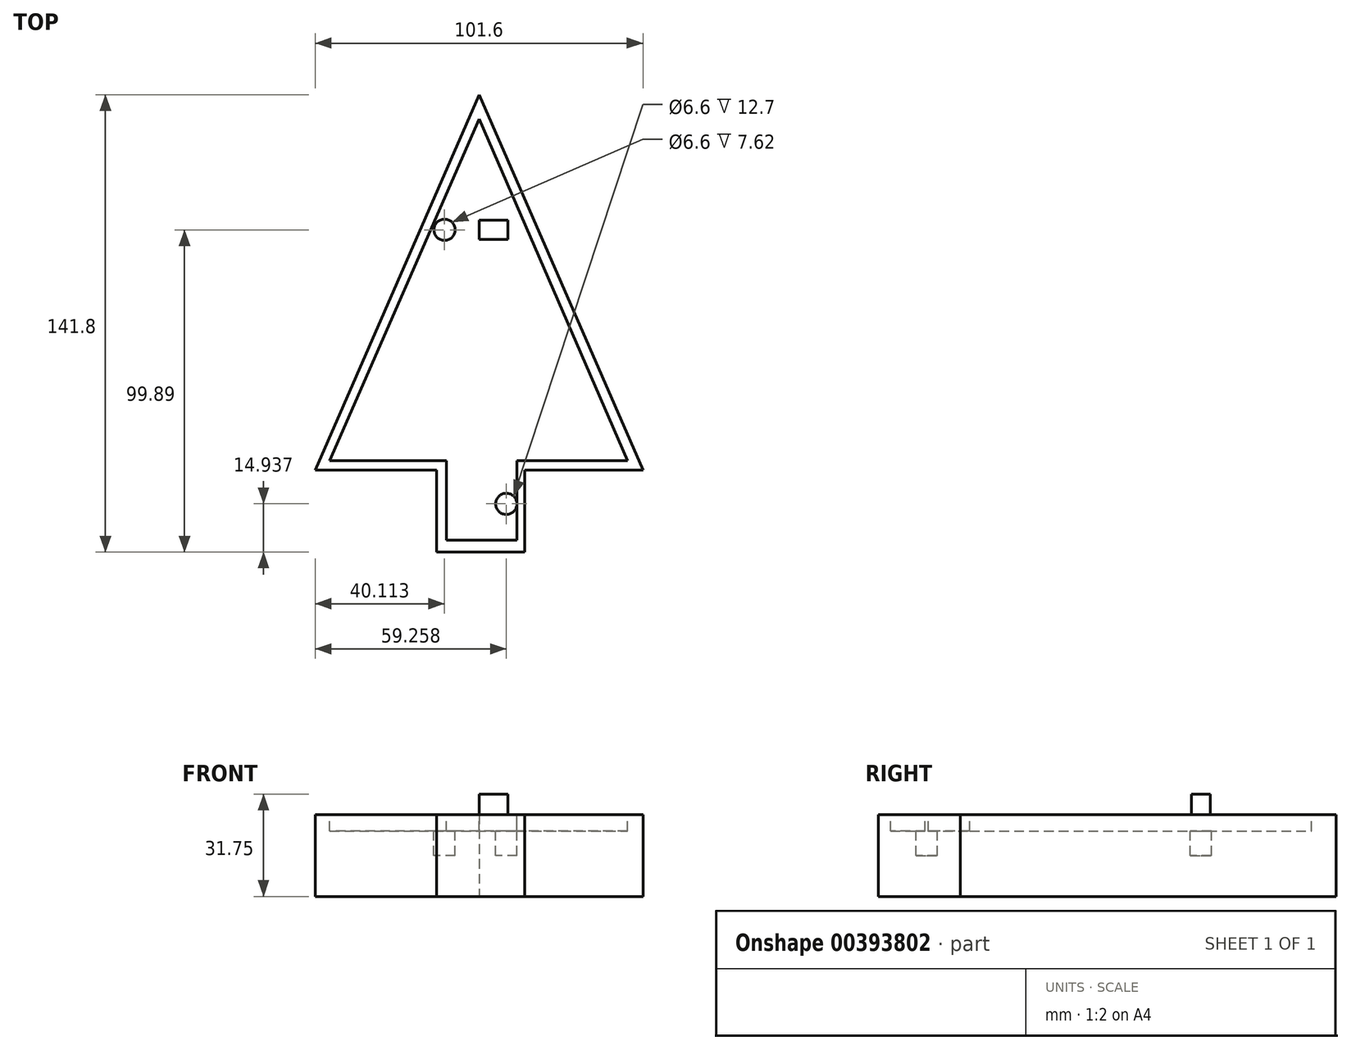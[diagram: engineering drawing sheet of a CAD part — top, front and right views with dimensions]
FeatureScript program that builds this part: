
annotation { "Feature Type Name" : "Feature", "Feature Type Description" : "" }
export const myFeature = defineFeature(function(context is Context, id is Id, definition is map)
    precondition{}
    {
        {
            var Q0;
            Q0=qCreatedBy(makeId("Top.planeOp"),FACE);
            var sketch = newSketch(context, id + "F0", { "sketchPlane" : qUnion([Q0])});
            skLineSegment(sketch, "E0", {"start": v(-50.8, -74.49) * mm, "end": v(50.8, -74.49) * mm});
            skLineSegment(sketch, "E1", {"start": v(-50.8, -74.49) * mm, "end": v(0, 41.91) * mm});
            skLineSegment(sketch, "E2", {"start": v(0, 41.91) * mm, "end": v(50.8, -74.49) * mm});
            skLineSegment(sketch, "E3", {"start": v(-13.2, -74.49) * mm, "end": v(-13.2, -99.89) * mm});
            skLineSegment(sketch, "E4", {"start": v(14.14, -74.49) * mm, "end": v(14.14, -99.89) * mm});
            skLineSegment(sketch, "E5", {"start": v(-13.2, -99.89) * mm, "end": v(14.14, -99.89) * mm});
            skSolve(sketch);
        }
        {
            var Q0;
            Q0 = qSketchRegion(id + "F0", true);
            extrude(context, id + "F1", {"entities" : qUnion([Q0]), "depth" : 25.4 * mm});
        }
        {
            var Q0;
            Q0=makeQuery(id+"F1.opExtrude","CAP_FACE",FACE,{"disambiguationData":[OSD([sQuery(id+"F0.wireOp",EDGE,"E0"),sQuery(id+"F0.wireOp",EDGE,"E1"),sQuery(id+"F0.wireOp",EDGE,"E2"),sQuery(id+"F0.wireOp",EDGE,"E3"),sQuery(id+"F0.wireOp",EDGE,"E4"),sQuery(id+"F0.wireOp",EDGE,"E5")])],"isStart":false});
            var sketch = newSketch(context, id + "F2", { "sketchPlane" : qUnion([Q0])});
            skCircle(sketch, "E6", {"center": v(8.46, -84.95) * mm, "radius": 3.3 * mm});
            skSolve(sketch);
        }
        {
            var Q0;
            Q0 = qSketchRegion(id + "F2", true);
            extrude(context, id + "F3", {"entities" : qUnion([Q0]), "operationType" : NewBodyOperationType.REMOVE, "oppositeDirection" : true, "depth" : 12.7 * mm});
        }
        {
            var Q0;
            Q0=makeQuery(id+"F1.opExtrude","CAP_FACE",FACE,{"disambiguationData":[OSD([sQuery(id+"F0.wireOp",EDGE,"E0"),sQuery(id+"F0.wireOp",EDGE,"E1"),sQuery(id+"F0.wireOp",EDGE,"E2"),sQuery(id+"F0.wireOp",EDGE,"E3"),sQuery(id+"F0.wireOp",EDGE,"E4"),sQuery(id+"F0.wireOp",EDGE,"E5")])],"isStart":false});
            var sketch = newSketch(context, id + "F4", { "sketchPlane" : qUnion([Q0])});
            skCircle(sketch, "E7", {"center": v(-10.69, 0) * mm, "radius": 3.3 * mm});
            skSolve(sketch);
        }
        {
            var Q0;
            Q0 = qSketchRegion(id + "F4", true);
            extrude(context, id + "F5", {"entities" : qUnion([Q0]), "operationType" : NewBodyOperationType.REMOVE, "oppositeDirection" : true, "depth" : 12.7 * mm});
        }
        {
            var Q0;
            Q0=makeQuery(id+"F1.opExtrude","CAP_FACE",FACE,{"disambiguationData":[OSD([sQuery(id+"F0.wireOp",EDGE,"E0"),sQuery(id+"F0.wireOp",EDGE,"E1"),sQuery(id+"F0.wireOp",EDGE,"E2"),sQuery(id+"F0.wireOp",EDGE,"E3"),sQuery(id+"F0.wireOp",EDGE,"E4"),sQuery(id+"F0.wireOp",EDGE,"E5")])],"isStart":false});
            var sketch = newSketch(context, id + "F6", { "sketchPlane" : qUnion([Q0])});
            skLineSegment(sketch, "E8.bottom", {"start": v(0, 2.94) * mm, "end": v(8.9, 2.94) * mm});
            skLineSegment(sketch, "E8.top", {"start": v(0, -2.94) * mm, "end": v(8.9, -2.94) * mm});
            skLineSegment(sketch, "E8.left", {"start": v(0, 2.94) * mm, "end": v(0, -2.94) * mm});
            skLineSegment(sketch, "E8.right", {"start": v(8.9, 2.94) * mm, "end": v(8.9, -2.94) * mm});
            skPoint(sketch, "E8.middle", {"position": v(4.45, 0) * mm});
            skSolve(sketch);
        }
        {
            var Q0;
            Q0 = qSketchRegion(id + "F6", true);
            extrude(context, id + "F7", {"entities" : qUnion([Q0]), "operationType" : NewBodyOperationType.ADD, "depth" : 6.35 * mm});
        }
        {
            var Q0;
            Q0=makeQuery(id+"F1.opExtrude","CAP_FACE",FACE,{"disambiguationData":[OSD([sQuery(id+"F0.wireOp",EDGE,"E0"),sQuery(id+"F0.wireOp",EDGE,"E1"),sQuery(id+"F0.wireOp",EDGE,"E2"),sQuery(id+"F0.wireOp",EDGE,"E3"),sQuery(id+"F0.wireOp",EDGE,"E4"),sQuery(id+"F0.wireOp",EDGE,"E5")])],"isStart":false});
            var sketch = newSketch(context, id + "F8", { "sketchPlane" : qUnion([Q0])});
            skLineSegment(sketch, "E9", {"start": v(0, 34.36) * mm, "end": v(-46.25, -71.62) * mm});
            skLineSegment(sketch, "E10", {"start": v(-46.25, -71.62) * mm, "end": v(-13.2, -71.62) * mm});
            skLineSegment(sketch, "E11", {"start": v(-13.2, -71.62) * mm, "end": v(-10.13, -71.62) * mm});
            skLineSegment(sketch, "E12", {"start": v(-10.13, -71.62) * mm, "end": v(-10.13, -96.16) * mm});
            skLineSegment(sketch, "E13", {"start": v(-10.13, -96.16) * mm, "end": v(11.72, -96.16) * mm});
            skLineSegment(sketch, "E14", {"start": v(11.72, -96.16) * mm, "end": v(11.72, -71.62) * mm});
            skLineSegment(sketch, "E15", {"start": v(11.72, -71.62) * mm, "end": v(46.03, -71.62) * mm});
            skLineSegment(sketch, "E16", {"start": v(46.03, -71.62) * mm, "end": v(0, 34.36) * mm});
            skSolve(sketch);
        }
        {
            var Q0;
            Q0 = qSketchRegion(id + "F8", true);
            extrude(context, id + "F9", {"entities" : qUnion([Q0]), "operationType" : NewBodyOperationType.REMOVE, "oppositeDirection" : true, "depth" : 5.08 * mm});
        }
    });
